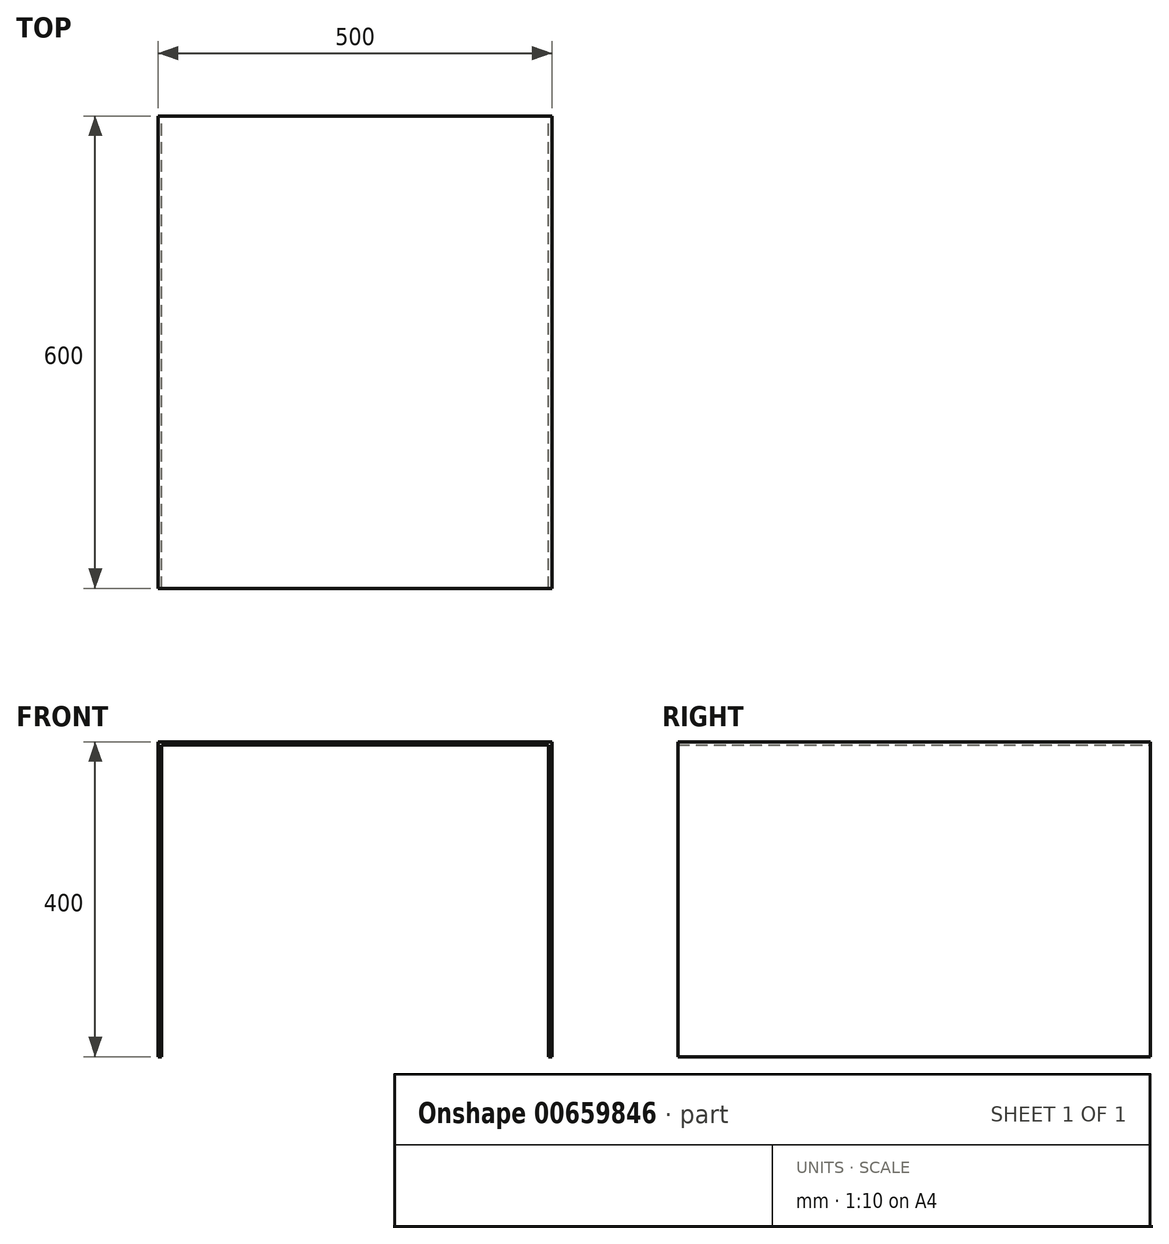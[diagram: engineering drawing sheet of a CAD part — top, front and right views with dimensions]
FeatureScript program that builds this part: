
annotation { "Feature Type Name" : "Feature", "Feature Type Description" : "" }
export const myFeature = defineFeature(function(context is Context, id is Id, definition is map)
    precondition{}
    {
        {
            var Q0;
            Q0=qCreatedBy(makeId("Front.planeOp"),FACE);
            var sketch = newSketch(context, id + "F0", { "sketchPlane" : qUnion([Q0])});
            skLineSegment(sketch, "E0", {"start": v(0, 0) * mm, "end": v(-250, 0) * mm});
            skLineSegment(sketch, "E1", {"start": v(-250, 0) * mm, "end": v(-250, -400) * mm});
            skLineSegment(sketch, "E2", {"start": v(-250, -400) * mm, "end": v(-246, -400) * mm});
            skLineSegment(sketch, "E3", {"start": v(-246, -400) * mm, "end": v(-246, -4) * mm});
            skLineSegment(sketch, "E4", {"start": v(-246, -4) * mm, "end": v(0, -4) * mm});
            skLineSegment(sketch, "E5.MirrorCS", {"start": v(0, 0) * mm, "end": v(250, 0) * mm});
            skLineSegment(sketch, "E6.MirrorCS", {"start": v(246, -4) * mm, "end": v(0, -4) * mm});
            skLineSegment(sketch, "E7.MirrorCS", {"start": v(246, -400) * mm, "end": v(246, -4) * mm});
            skLineSegment(sketch, "E8.MirrorCS", {"start": v(250, 0) * mm, "end": v(250, -400) * mm});
            skLineSegment(sketch, "E9.MirrorCS", {"start": v(250, -400) * mm, "end": v(246, -400) * mm});
            skSolve(sketch);
        }
        {
            var Q0;
            Q0 = qSketchRegion(id + "F0", true);
            extrude(context, id + "F1", {"entities" : qUnion([Q0]), "depth" : 600 * mm, "offsetDistance" : 25 * mm});
        }
    });
